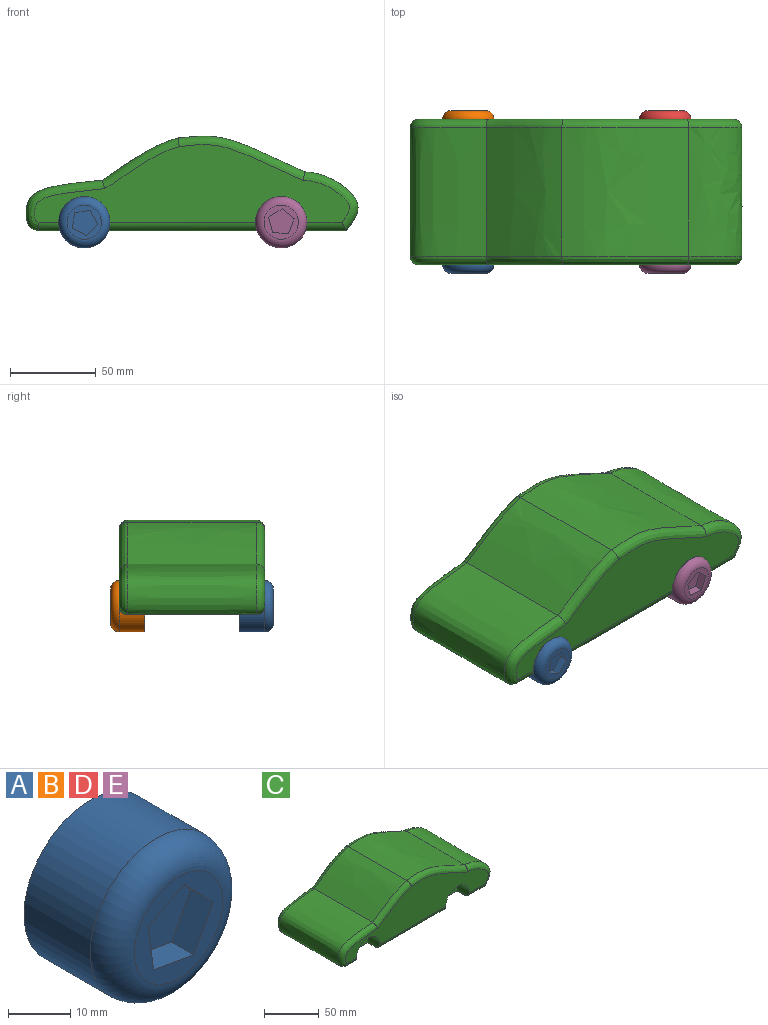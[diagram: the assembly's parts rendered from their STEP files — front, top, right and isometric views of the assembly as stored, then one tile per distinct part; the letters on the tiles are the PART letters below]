
ASSEMBLY  parts=5 mates=4
PART A: 10 faces, bbox 32.5x20x32.5 mm
  f0: cylinder r=15mm len=30mm, axis (0,1,0), area 1413.7mm2, adj f2,f3
  f1: plane 20x20mm, normal (0,-1,0), area 167.1mm2, adj f3,f4,f5,f6,f7,f8
  f2: plane 30x30mm, normal (0,1,0), area 706.9mm2, adj f0
  f3: torus R=10mm, axis (0,-1,0), area 650.6mm2, adj f0,f1
  f4: plane 8.15x5mm, normal (-0.88,0,0.47), area 46.2mm2, adj f1,f5,f8,f9
  f5: plane 6.66x6.41mm, normal (-0.72,0,-0.69), area 46.2mm2, adj f1,f4,f6,f9
  f6: plane 8.32x5mm, normal (0.44,0,-0.9), area 46.2mm2, adj f1,f5,f7,f9
  f7: plane 9.16x5mm, normal (0.99,0,0.14), area 46.2mm2, adj f1,f6,f8,f9
  f8: plane 9.1x5mm, normal (0.18,0,0.98), area 46.2mm2, adj f1,f4,f7,f9
  f9: plane 14.82x14.73mm, normal (0,-1,0), area 147.1mm2, adj f4,f5,f6,f7,f8
PART B: same geometry as A
PART C: 29 faces, bbox 194x85x56 mm
  f0: plane 180x75mm, normal (0,0,-1), area 12368.6mm2, adj f2,f3,f4,f5,f6,f9,f10,f16
  f1: plane 183.93x45.32mm, normal (0,1,0), area 4731.2mm2, adj f2,f3,f4,f17,f18,f19,f20,f26
  f2: cylinder r=5mm len=12.84mm, axis (1,0,0), area 95.2mm2, adj f0,f1,f19,f28
  f3: cylinder r=5mm len=86.72mm, axis (1,0,0), area 674.3mm2, adj f0,f1,f26,f28
  f4: cylinder r=5mm len=23.87mm, axis (1,0,0), area 174.4mm2, adj f0,f1,f20,f26
  f5: cylinder r=5mm len=12.84mm, axis (-1,0,0), area 95.2mm2, adj f0,f11,f14,f24
  f6: cylinder r=5mm len=86.72mm, axis (-1,0,0), area 674.3mm2, adj f0,f11,f22,f24
  f7: extruded ~75x74.1mm, area 5867.1mm2, adj f8,f10,f13,f18
  f8: extruded ~75x44.29mm, area 3821.2mm2, adj f7,f9,f12,f17
  f9: extruded ~75x44.44mm, area 5055.7mm2, adj f0,f8,f14,f19
  f10: extruded ~75x34.46mm, area 4163.8mm2, adj f0,f7,f15,f20
  f11: plane 183.94x45.31mm, normal (0,-1,0), area 4731.2mm2, adj f5,f6,f12,f13,f14,f15,f16,f22
  f12: bspline ~47.12x29.87mm, area 399mm2, adj f8,f11,f13,f14
  f13: bspline ~76.59x26.03mm, area 609.6mm2, adj f7,f11,f12,f15
  f14: bspline ~50.8x30.17mm, area 492.5mm2, adj f5,f9,f11,f12
  f15: bspline ~35.2x34.11mm, area 398.6mm2, adj f10,f11,f13,f16
  f16: cylinder r=5mm len=23.87mm, axis (-1,0,0), area 174.4mm2, adj f0,f11,f15,f22
  f17: bspline ~47.12x29.87mm, area 399mm2, adj f1,f8,f18,f19
  f18: bspline ~76.59x26.03mm, area 609.6mm2, adj f1,f7,f17,f20
  f19: bspline ~50.8x30.17mm, area 492.5mm2, adj f1,f2,f9,f17
  f20: bspline ~35.2x34.11mm, area 398.6mm2, adj f1,f4,f10,f18
  f21: plane 30x20mm, normal (0,-1,0), area 500.6mm2, adj f0,f22
  f22: cylinder r=15mm len=30mm, axis (0,-1,0), area 834.3mm2, adj f0,f6,f11,f16,f21
  f23: plane 30x20mm, normal (0,-1,0), area 500.6mm2, adj f0,f24
  f24: cylinder r=15mm len=30mm, axis (0,-1,0), area 834.3mm2, adj f0,f5,f6,f11,f23
  f25: plane 30x20mm, normal (0,1,0), area 500.6mm2, adj f0,f26
  f26: cylinder r=15mm len=30mm, axis (0,1,0), area 834.3mm2, adj f0,f1,f3,f4,f25
  f27: plane 30x20mm, normal (0,1,0), area 500.6mm2, adj f0,f28
  f28: cylinder r=15mm len=30mm, axis (0,1,0), area 834.3mm2, adj f0,f1,f2,f3,f27
PART D: same geometry as A
PART E: same geometry as A
PLACE A rot(axis=(0,1,0),16.7deg) t=(-66.97,-62.7,4.86)mm
PLACE B rot(axis=(0,0,-1),180deg) t=(-66.97,-7.7,4.86)mm
PLACE C t=(-4.52,7.3,-0.14)mm fixed
PLACE D rot(axis=(-0.71,0,0.71),180deg) t=(48.03,-7.7,4.86)mm
PLACE E rot(axis=(0,1,0),65.6deg) t=(48.03,-62.7,4.86)mm
MATE revolute E.f0 <-> C.f22  axis (0,1,0) through (48.03,-62.7,4.86)mm
MATE revolute B.f0 <-> C.f24  axis (0,-1,0) through (-66.97,-7.7,4.86)mm
MATE revolute D.f0 <-> C.f22  axis (0,-1,0) through (48.03,-7.7,4.86)mm
MATE revolute A.f0 <-> C.f24  axis (0,1,0) through (-66.97,-62.7,4.86)mm
